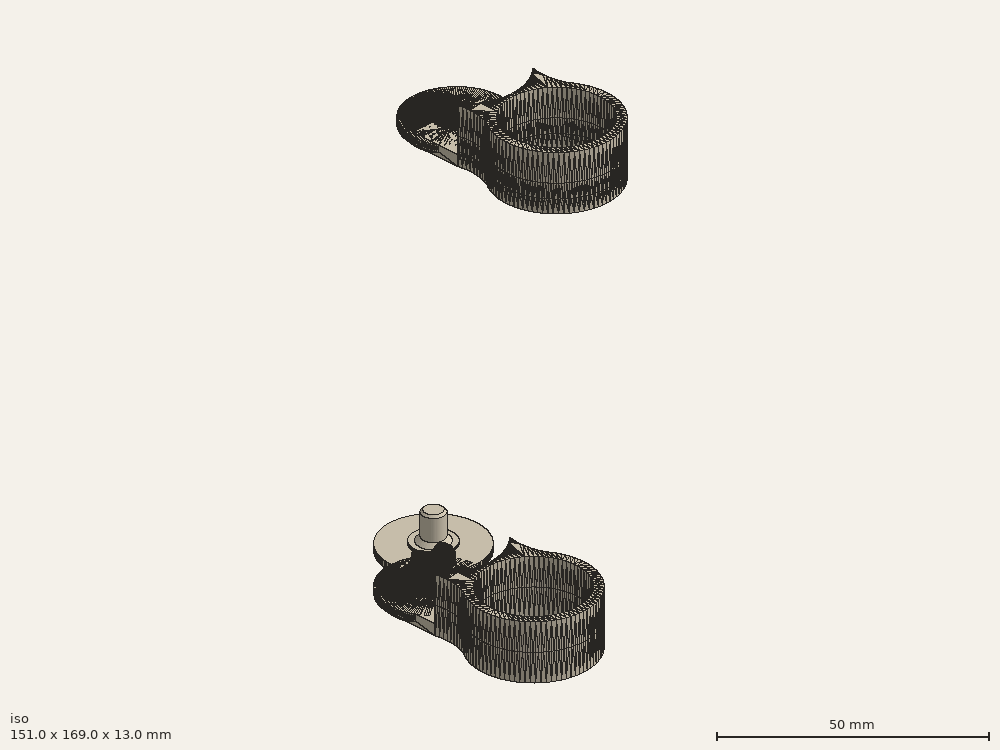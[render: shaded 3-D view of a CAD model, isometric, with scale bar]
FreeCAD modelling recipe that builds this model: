
FCSTD DOCUMENT  (FreeCAD 1.0R39319 (Git))
Label: Spinner_Fidget_Fix
License: All rights reserved
LicenseURL: https://en.wikipedia.org/wiki/All_rights_reserved
objects: Part::Feature×6, Sketcher::SketchObject×4, Mesh::Feature×3, PartDesign::FeatureBase×2, PartDesign::Chamfer×2, PartDesign::Body×2, PartDesign::Pocket×1, PartDesign::Pad×1
note: 32 computed .brp shape members not serialized (recipe doc carries the construction recipe); baked Part::Feature solids carry a one-line shape summary decoded from their .brp

FEATURE [Mesh::Feature] yogi_button_screw  label="yogi-button-screw"
FEATURE [Part::Feature] yogi_button_screw001
  shape: bbox 22 x 22 x 9.75 mm, 21468 faces, 0 solids (baked)
FEATURE [Part::Feature] yogi_button_screw001_solid  label="yogi_button_screw001 (Solid)"
  shape: bbox 22 x 22 x 9.75 mm, 21468 faces (baked)
FEATURE [Mesh::Feature] yogi_fidget_case  label="yogi-fidget-case"
FEATURE [Part::Feature] yogi_fidget_case001
  shape: bbox 25.99 x 50 x 12.99 mm, 23408 faces, 0 solids (baked)
FEATURE [Part::Feature] yogi_fidget_case001_solid  label="yogi_fidget_case001 (Solid)"
  shape: bbox 25.99 x 50 x 12.99 mm, 23408 faces (baked)
FEATURE [PartDesign::FeatureBase] BaseFeature
  BaseFeature = -> yogi_button_screw001_solid
  Suppressed = false
FEATURE [Sketcher::SketchObject] Sketch
  ArcFitTolerance = 1e-06
  AttachmentSupport = -> [BaseFeature]
  ExternalGeometry = -> [BaseFeature]
  FullyConstrained = true
  MakeInternals = false
  MapMode = 5
  Placement = pos=(0,0,3.15) rot=(0,0,1;0rad)
  sketch-geometry (2):
    g0: Circle [constr] CenterX=11 CenterY=11 CenterZ=0 NormalX=0 NormalY=0 NormalZ=1 AngleXU=0 Radius=11
    g1: Circle CenterX=11 CenterY=11 CenterZ=0 NormalX=0 NormalY=0 NormalZ=1 AngleXU=0 Radius=5
  constraints (5):
    c: PointOnObject(g-3,g0)
    c: PointOnObject(g-3,g0)
    c: PointOnObject(g-4,g0)
    c: Coincident(g1,g0)
    c: Diameter(g1) = 10
FEATURE [PartDesign::Pocket] Pocket
  BaseFeature = -> BaseFeature
  Direction = (0,0,-1)
  Length = 10
  Length2 = 5
  Profile = -> Sketch
  ReferenceAxis = -> Sketch [N_Axis]
  Refine = true
  Reversed = true
  Suppressed = false
  Type = 0
FEATURE [Sketcher::SketchObject] Sketch001
  ArcFitTolerance = 1e-06
  AttachmentSupport = -> [Pocket]
  ExternalGeometry = -> [Pocket]
  FullyConstrained = true
  MakeInternals = false
  MapMode = 5
  Placement = pos=(0,0,3.15) rot=(0,0,1;0rad)
  expr: Constraints[3] = 8 - 2 * 1.5
  sketch-geometry (2):
    g0: Circle [constr] CenterX=11 CenterY=11 CenterZ=0 NormalX=0 NormalY=0 NormalZ=1 AngleXU=0 Radius=4.75
    g1: Circle CenterX=11 CenterY=11 CenterZ=0 NormalX=0 NormalY=0 NormalZ=1 AngleXU=0 Radius=2.5
  constraints (5):
    c: PointOnObject(g-3,g0)
    c: PointOnObject(g-3,g0)
    c: PointOnObject(g-4,g0)
    c: Diameter(g1) = 5
    c: Coincident(g1,g0)
FEATURE [PartDesign::Pad] Pad
  BaseFeature = -> Pocket
  Direction = (0,0,1)
  Length = 6.6
  Length2 = 10
  Profile = -> Sketch001
  ReferenceAxis = -> Sketch001 [N_Axis]
  Refine = true
  Suppressed = false
  Type = 0
FEATURE [PartDesign::Chamfer] Chamfer
  Angle = 45
  Base = -> Pad [Edge363]
  BaseFeature = -> Pad
  ChamferType = 0
  FlipDirection = false
  Refine = true
  Size = 0.5
  Size2 = 1
  SupportTransform = false
  Suppressed = false
  UseAllEdges = false
FEATURE [PartDesign::Chamfer] Chamfer001
  Angle = 45
  Base = -> Chamfer [Edge3]
  BaseFeature = -> Chamfer
  ChamferType = 0
  FlipDirection = false
  Refine = true
  Size = 1
  Size2 = 1
  SupportTransform = false
  Suppressed = false
  UseAllEdges = false
FEATURE [PartDesign::Body] Body  label="button-screw"
  AllowCompound = false
  BaseFeature = -> yogi_button_screw001_solid
  Group = -> [BaseFeature,Sketch,Pocket,Sketch001,Pad,Chamfer,Chamfer001]
  Origin = -> Origin
  Tip = -> Chamfer001
FEATURE [Mesh::Feature] yogi_fidget_case_cut  label="yogi-fidget-case-cut"
FEATURE [Part::Feature] yogi_fidget_case_cut001
  shape: bbox 25.99 x 50 x 12.99 mm, 6044 faces, 0 solids (baked)
FEATURE [Part::Feature] yogi_fidget_case_cut001_solid  label="yogi_fidget_case_cut001 (Solid)"
  shape: bbox 25.99 x 50 x 12.99 mm, 6044 faces (baked)
FEATURE [PartDesign::FeatureBase] BaseFeature001
  BaseFeature = -> yogi_fidget_case_cut001_solid
  Suppressed = false
FEATURE [Sketcher::SketchObject] Sketch002
  ArcFitTolerance = 1e-06
  AttachmentSupport = -> [BaseFeature001]
  ExternalGeometry = -> [BaseFeature001]
  FullyConstrained = true
  MakeInternals = false
  MapMode = 5
  Placement = pos=(0,0,3.15) rot=(0,0,1;0rad)
  expr: Constraints[5] = 8 - 2 * 1.5
  sketch-geometry (3):
    g0: Circle [constr] CenterX=125.002 CenterY=119.001 CenterZ=0 NormalX=0 NormalY=0 NormalZ=1 AngleXU=0 Radius=4.75007
    g1: Circle CenterX=125.002 CenterY=119.001 CenterZ=0 NormalX=0 NormalY=0 NormalZ=1 AngleXU=0 Radius=4
    g2: Circle CenterX=125.002 CenterY=119.001 CenterZ=0 NormalX=0 NormalY=0 NormalZ=1 AngleXU=0 Radius=2.5
  constraints (7):
    c: PointOnObject(g-3,g0)
    c: PointOnObject(g-3,g0)
    c: PointOnObject(g-4,g0)
    c: Diameter(g1) = 8
    c: Coincident(g1,g0)
    c: Diameter(g2) = 5
    c: Coincident(g2,g0)
FEATURE [Sketcher::SketchObject] Sketch003
  ArcFitTolerance = 1e-06
  AttachmentSupport = -> [XY_Plane001]
  ExternalGeometry = -> [Sketch002]
  FullyConstrained = true
  MakeInternals = false
  MapMode = 5
  expr: Constraints[2] = 8 - 2 * 1.5
  sketch-geometry (2):
    g0: Circle CenterX=125.002 CenterY=119.001 CenterZ=0 NormalX=0 NormalY=0 NormalZ=1 AngleXU=0 Radius=4
    g1: Circle CenterX=125.002 CenterY=119.001 CenterZ=0 NormalX=0 NormalY=0 NormalZ=1 AngleXU=0 Radius=2.5
  constraints (4):
    c: Coincident(g0,g-3)
    c: Equal(g0,g-3)
    c: Diameter(g1) = 5
    c: Coincident(g1,g0)
FEATURE [PartDesign::Body] Body001  label="fidget-case"
  AllowCompound = false
  BaseFeature = -> yogi_fidget_case_cut001_solid
  Group = -> [BaseFeature001,Sketch002,Sketch003]
  Origin = -> Origin001
  Tip = -> BaseFeature001
